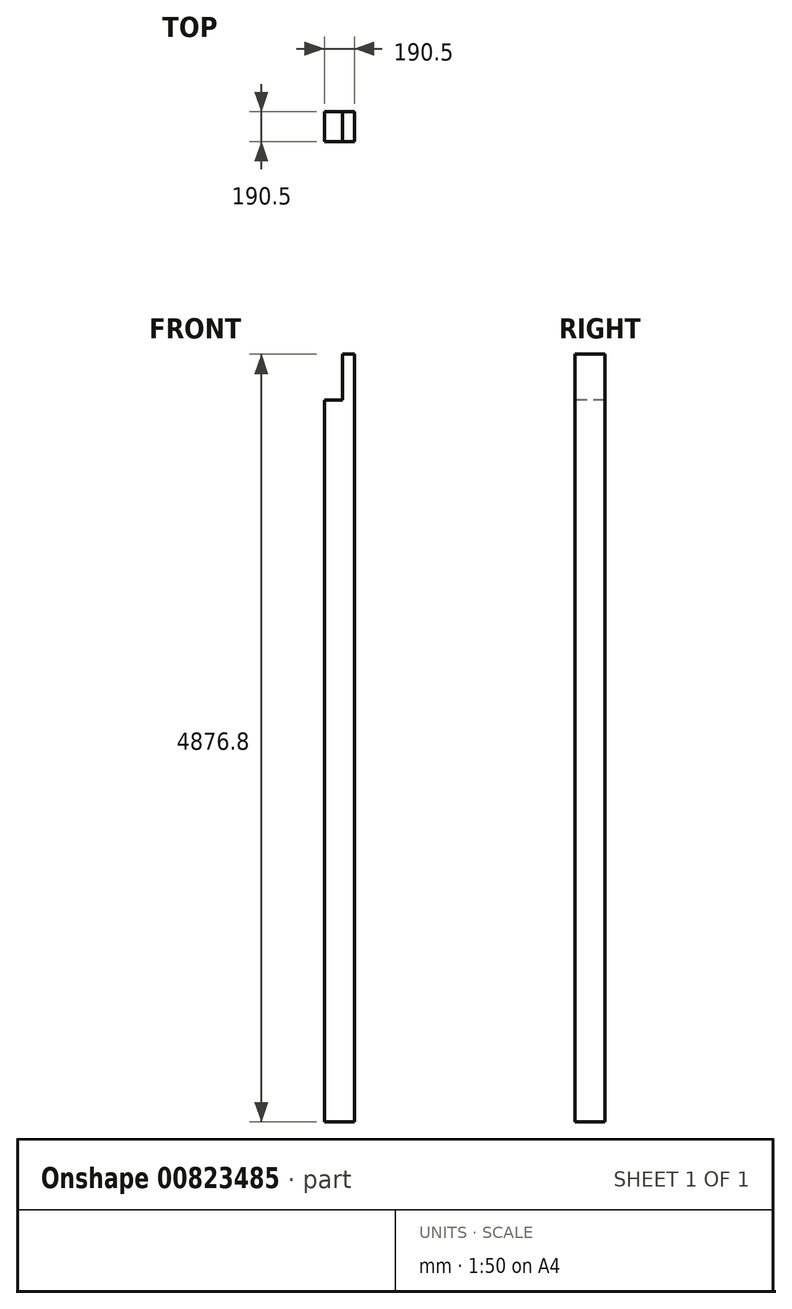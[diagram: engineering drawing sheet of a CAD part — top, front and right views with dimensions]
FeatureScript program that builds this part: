
annotation { "Feature Type Name" : "Feature", "Feature Type Description" : "" }
export const myFeature = defineFeature(function(context is Context, id is Id, definition is map)
    precondition{}
    {
        {
            var Q0;
            Q0=qCreatedBy(makeId("Top.planeOp"),FACE);
            var sketch = newSketch(context, id + "F0", { "sketchPlane" : qUnion([Q0])});
            skLineSegment(sketch, "E0.bottom", {"start": v(-95.25, -95.25) * mm, "end": v(95.25, -95.25) * mm});
            skLineSegment(sketch, "E0.top", {"start": v(-95.25, 95.25) * mm, "end": v(95.25, 95.25) * mm});
            skLineSegment(sketch, "E0.left", {"start": v(-95.25, -95.25) * mm, "end": v(-95.25, 95.25) * mm});
            skLineSegment(sketch, "E0.right", {"start": v(95.25, -95.25) * mm, "end": v(95.25, 95.25) * mm});
            skSolve(sketch);
        }
        {
            var Q0;
            Q0 = qSketchRegion(id + "F0", true);
            extrude(context, id + "F1", {"entities" : qUnion([Q0]), "depth" : 4876.8 * mm, "offsetDistance" : 25.4 * mm});
        }
        {
            var Q0;
            Q0=makeQuery(id+"F1.opExtrude","SWEPT_FACE",FACE,{"disambiguationData":[OSD([sQuery(id+"F0.wireOp",EDGE,"E0.bottom")])]});
            var sketch = newSketch(context, id + "F2", { "sketchPlane" : qUnion([Q0])});
            skLineSegment(sketch, "E1.bottom", {"start": v(-95.25, 4876.8) * mm, "end": v(19.05, 4876.8) * mm});
            skLineSegment(sketch, "E1.top", {"start": v(-95.25, 4584.7) * mm, "end": v(19.05, 4584.7) * mm});
            skLineSegment(sketch, "E1.left", {"start": v(-95.25, 4876.8) * mm, "end": v(-95.25, 4584.7) * mm});
            skLineSegment(sketch, "E1.right", {"start": v(19.05, 4876.8) * mm, "end": v(19.05, 4584.7) * mm});
            skSolve(sketch);
        }
        {
            var Q0;
            Q0 = qSketchRegion(id + "F2", true);
            extrude(context, id + "F3", {"entities" : qUnion([Q0]), "operationType" : NewBodyOperationType.REMOVE, "endBound" : BoundingType.THROUGH_ALL, "oppositeDirection" : true, "depth" : 25.4 * mm, "offsetDistance" : 25.4 * mm});
        }
    });
